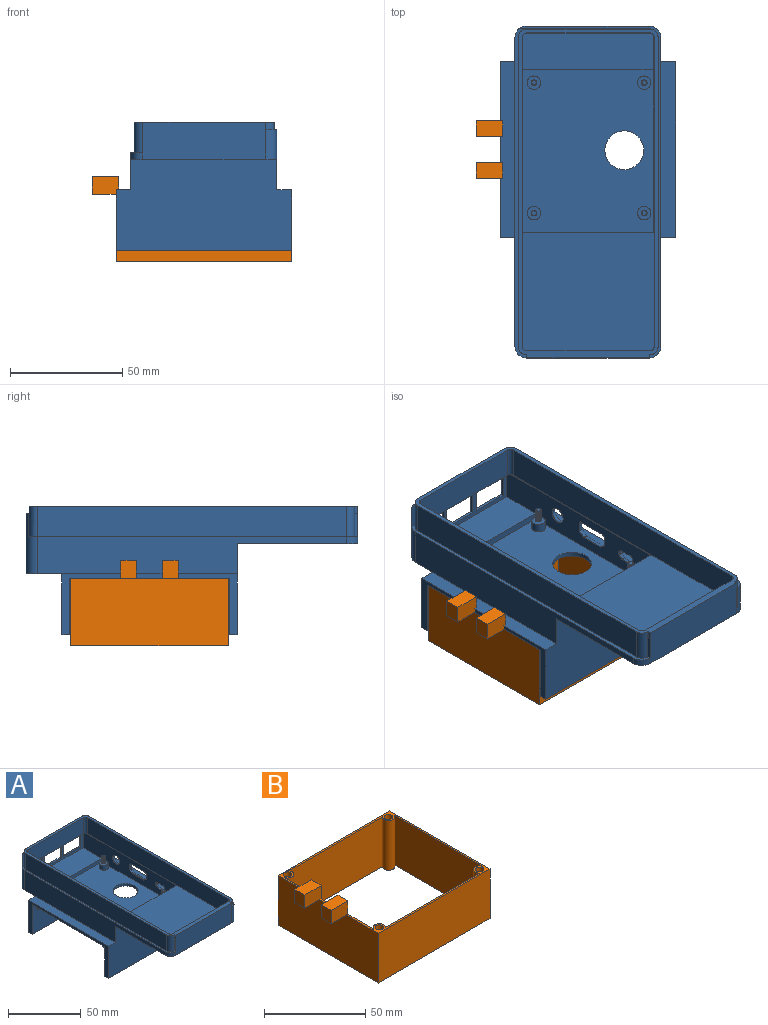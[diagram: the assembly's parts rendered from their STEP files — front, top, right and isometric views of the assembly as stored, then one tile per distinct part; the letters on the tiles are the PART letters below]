
ASSEMBLY  parts=2 mates=1
PART A: 172 faces, bbox 78.1x147.8x57.3 mm
  f0: plane 54.64x26.93mm, normal (0,1,0), area 672.3mm2, adj f70,f71,f72,f73,f74,f75,f76,f77
  f1: plane 10.44x0.05mm, normal (1,0,0), area 0.5mm2, adj f6,f156,f161,f168
  f2: plane 146.29x62.14mm, normal (0,0,1), area 777.6mm2, adj f3,f142,f143,f144,f145,f146,f147,f148
  f3: plane 54.77x16.64mm, normal (0,-1,0), area 908.8mm2, adj f2,f4,f5,f138,f139,f140,f163,f164
  f4: plane 10.44x1.35mm, normal (-1,0,0), area 14.1mm2, adj f3,f5,f147,f166
  f5: plane 146.45x5.23mm, normal (0,0,1), area 219.8mm2, adj f3,f4,f13,f69,f87,f136,f139,f145
  f6: plane 144.71x3.8mm, normal (0,0,1), area 7.4mm2, adj f1,f8,f142,f143,f156,f159,f160,f161
  f7: plane 137.44x26.93mm, normal (1,0,0), area 2509mm2, adj f10,f22,f70,f112,f113,f114,f115,f116
  f8: plane 90.66x16.5mm, normal (-1,0,0), area 1254.4mm2, adj f6,f9,f11,f12,f13,f83,f85,f88
  f9: plane 58.23x18.21mm, normal (0,0,1), area 1060.3mm2, adj f8,f12,f13,f87
  f10: plane 78x6.58mm, normal (0,0,1), area 513.2mm2, adj f7,f14,f20,f22
  f11: plane 72.45x58.92mm, normal (0,0,1), area 3922.5mm2, adj f8,f12,f44,f45,f46,f47,f68,f83
  f12: plane 58.92x3mm, normal (0,-1,0), area 176.8mm2, adj f8,f9,f11,f84,f86
  f13: plane 59.61x23.93mm, normal (0,-1,0), area 592.4mm2, adj f5,f8,f9,f71,f72,f73,f74,f75
  f14: plane 78x27mm, normal (0,1,0), area 2106mm2, adj f10,f20,f21,f23,f43,f70
  f15: plane 6.13x6.13mm, normal (0,0,1), area 24.4mm2, adj f44,f63,f65,f66,f67
  f16: plane 6.13x6.13mm, normal (0,0,1), area 24.4mm2, adj f46,f58,f60,f61,f62
  f17: plane 6.13x6.13mm, normal (0,0,1), area 24.4mm2, adj f47,f53,f55,f56,f57
  f18: plane 6.13x6.13mm, normal (0,0,1), area 24.4mm2, adj f45,f48,f50,f51,f52
  f19: plane 78x71mm, normal (0,0,-1), area 5254.4mm2, adj f20,f21,f24,f26,f32,f34,f40,f42
  f20: plane 78x27mm, normal (1,0,0), area 331mm2, adj f10,f14,f19,f22,f40,f41,f42,f43
  f21: plane 78x27mm, normal (-1,0,0), area 331mm2, adj f14,f19,f22,f23,f40,f41,f42,f43
  f22: plane 78x40.5mm, normal (0,-1,0), area 2981.2mm2, adj f7,f10,f20,f21,f23,f41,f69,f138
  f23: plane 78x6.58mm, normal (0,0,1), area 513.2mm2, adj f14,f21,f22,f69
  f24: cylinder r=2mm len=7mm, axis (0,0,1), area 88mm2, adj f19,f25
  f25: plane 4x4mm, normal (0,0,-1), area 10.6mm2, adj f24,f31
  f26: cylinder r=2mm len=7mm, axis (0,0,1), area 88mm2, adj f19,f27
  f27: plane 4x4mm, normal (0,0,-1), area 10.6mm2, adj f26,f29
  f28: cone r=0mm half-angle=59deg, axis (0,0,-1), area 2.3mm2, adj f29
  f29: cylinder r=0.8mm len=5.85mm, axis (0,0,-1), area 29.4mm2, adj f27,f28
  f30: cone r=0mm half-angle=59deg, axis (0,0,-1), area 2.3mm2, adj f31
  f31: cylinder r=0.8mm len=5.85mm, axis (0,0,-1), area 29.4mm2, adj f25,f30
  f32: cylinder r=2mm len=4mm, axis (0,0,1), area 37.7mm2, adj f19,f33
  f33: plane 4x4mm, normal (0,0,-1), area 10.6mm2, adj f32,f39
  f34: cylinder r=2mm len=4mm, axis (0,0,1), area 37.7mm2, adj f19,f35
  f35: plane 4x4mm, normal (0,0,-1), area 10.6mm2, adj f34,f37
  f36: cone r=0mm half-angle=59deg, axis (0,0,-1), area 2.3mm2, adj f37
  f37: cylinder r=0.8mm len=4mm, axis (0,0,-1), area 20.1mm2, adj f35,f36
  f38: cone r=0mm half-angle=59deg, axis (0,0,-1), area 2.3mm2, adj f39
  f39: cylinder r=0.8mm len=4mm, axis (0,0,-1), area 20.1mm2, adj f33,f38
  f40: plane 78x25mm, normal (0,1,0), area 1950mm2, adj f19,f20,f21,f41
  f41: plane 78x3.5mm, normal (0,0,-1), area 273mm2, adj f20,f21,f22,f40
  f42: plane 78x25mm, normal (0,-1,0), area 1950mm2, adj f19,f20,f21,f43
  f43: plane 78x3.5mm, normal (0,0,-1), area 273mm2, adj f14,f20,f21,f42
  f44: cylinder r=3mm len=6mm, axis (0,0,-1), area 75.4mm2, adj f11,f15
  f45: cylinder r=3mm len=6mm, axis (0,0,-1), area 75.4mm2, adj f11,f18
  f46: cylinder r=3mm len=6mm, axis (0,0,-1), area 75.4mm2, adj f11,f16
  f47: cylinder r=3mm len=6mm, axis (0,0,-1), area 75.4mm2, adj f11,f17
  f48: cylinder r=1.25mm len=6mm, axis (0,0,-1), area 27.4mm2, adj f18,f49,f50,f52
  f49: plane 2.35x2.35mm, normal (0,0,1), area 3.9mm2, adj f48,f50,f51,f52
  f50: bspline ~6.28x2.5mm, area 26.8mm2, adj f18,f48,f49,f51
  f51: cylinder r=1.01mm len=6mm, axis (0,0,-1), area -6.5mm2, adj f18,f49,f50,f52
  f52: bspline ~6.28x2.5mm, area 26.3mm2, adj f18,f48,f49,f51
  f53: cylinder r=1.25mm len=6mm, axis (0,0,-1), area 27.4mm2, adj f17,f54,f55,f57
  f54: plane 2.35x2.35mm, normal (0,0,1), area 3.9mm2, adj f53,f55,f56,f57
  f55: bspline ~6.28x2.5mm, area 26.8mm2, adj f17,f53,f54,f56
  f56: cylinder r=1.01mm len=6mm, axis (0,0,-1), area -6.5mm2, adj f17,f54,f55,f57
  f57: bspline ~6.28x2.5mm, area 26.3mm2, adj f17,f53,f54,f56
  f58: cylinder r=1.25mm len=6mm, axis (0,0,-1), area 27.4mm2, adj f16,f59,f60,f62
  f59: plane 2.35x2.35mm, normal (0,0,1), area 3.9mm2, adj f58,f60,f61,f62
  f60: bspline ~6.28x2.5mm, area 26.8mm2, adj f16,f58,f59,f61
  f61: cylinder r=1.01mm len=6mm, axis (0,0,-1), area -6.5mm2, adj f16,f59,f60,f62
  f62: bspline ~6.28x2.5mm, area 26.3mm2, adj f16,f58,f59,f61
  f63: cylinder r=1.25mm len=6mm, axis (0,0,-1), area 27.4mm2, adj f15,f64,f65,f67
  f64: plane 2.35x2.35mm, normal (0,0,1), area 3.9mm2, adj f63,f65,f66,f67
  f65: bspline ~6.28x2.5mm, area 26.8mm2, adj f15,f63,f64,f66
  f66: cylinder r=1.01mm len=6mm, axis (0,0,-1), area -6.5mm2, adj f15,f64,f65,f67
  f67: bspline ~6.28x2.5mm, area 26.3mm2, adj f15,f63,f64,f66
  f68: cylinder r=8.62mm len=17.24mm, axis (0,0,1), area 108.3mm2, adj f11,f19
  f69: plane 137.44x16.5mm, normal (-1,0,0), area 1611.1mm2, adj f5,f22,f23,f70,f136,f138,f139
  f70: plane 64.84x15.91mm, normal (0,0,-1), area 1020.3mm2, adj f0,f7,f14,f69,f136,f137
  f71: plane 17x1.2mm, normal (-1,0,0), area 20.4mm2, adj f0,f13,f72,f73
  f72: plane 16.28x1.2mm, normal (0,0,-1), area 19.5mm2, adj f0,f13,f71,f74
  f73: plane 16.4x1.2mm, normal (0,0,1), area 19.6mm2, adj f0,f13,f71,f74
  f74: plane 17x1.2mm, normal (1,0,-0.01), area 20.4mm2, adj f0,f13,f72,f73
  f75: plane 16.28x1.2mm, normal (0,0,-1), area 19.5mm2, adj f0,f13,f76,f77
  f76: plane 17x1.2mm, normal (1,0,0), area 20.4mm2, adj f0,f13,f75,f78
  f77: plane 17x1.2mm, normal (-1,0,0), area 20.4mm2, adj f0,f13,f75,f78
  f78: plane 16.29x1.2mm, normal (0,0,1), area 19.5mm2, adj f0,f13,f76,f77
  f79: plane 14.5x1.2mm, normal (1,0,0), area 17.4mm2, adj f0,f13,f80,f82
  f80: plane 16.88x1.2mm, normal (0,0,-1), area 20.2mm2, adj f0,f13,f79,f81
  f81: plane 14.5x1.2mm, normal (-1,0,0), area 17.4mm2, adj f0,f13,f80,f82
  f82: plane 16.88x1.2mm, normal (0,0,1), area 20.2mm2, adj f0,f13,f79,f81
  f83: plane 58.92x16.5mm, normal (0,1,0), area 962.7mm2, adj f8,f11,f84,f85,f86,f87,f141
  f84: plane 72.45x3mm, normal (1,0,0), area 217.3mm2, adj f11,f12,f83,f86
  f85: plane 140.7x58.64mm, normal (0,0,1), area 3126.7mm2, adj f8,f83,f148,f149,f150,f151,f152,f153
  f86: plane 72.45x0.7mm, normal (0,0,-1), area 50.6mm2, adj f12,f83,f84,f87
  f87: plane 90.66x13.5mm, normal (1,0,0), area 1223.8mm2, adj f5,f9,f13,f83,f86,f141
  f88: plane 1.91x0.42mm, normal (0,0,-1), area 0.8mm2, adj f8,f89,f134
  f89: cylinder r=3.48mm len=6.95mm, axis (1,0,0), area 8.3mm2, adj f8,f88,f135
  f90: cylinder r=1.5mm len=1.5mm, axis (1,0,0), area 1mm2, adj f8,f91,f95,f128
  f91: plane 12.99x0.42mm, normal (0,0,-1), area 5.4mm2, adj f8,f90,f92,f126
  f92: cylinder r=1.5mm len=1.5mm, axis (1,0,0), area 1mm2, adj f8,f91,f93,f127
  f93: plane 4.06x0.42mm, normal (0,1,0), area 1.7mm2, adj f8,f92,f94,f129
  f94: plane 2.59x1.94mm, normal (0,0.6,0.8), area 1.3mm2, adj f8,f93,f96,f131
  f95: plane 4.06x0.42mm, normal (0,-1,0), area 1.7mm2, adj f8,f90,f97,f130
  f96: plane 10.81x0.42mm, normal (0,0,1), area 4.5mm2, adj f8,f94,f97,f133
  f97: plane 2.59x1.94mm, normal (0,-0.6,0.8), area 1.3mm2, adj f8,f95,f96,f132
  f98: plane 5.68x0.42mm, normal (0,0,1), area 2.4mm2, adj f8,f99,f111,f123
  f99: plane 1.54x1.21mm, normal (0,-0.79,0.62), area 0.8mm2, adj f8,f98,f100,f125
  f100: cylinder r=1mm len=0.62mm, axis (1,0,0), area 0.3mm2, adj f8,f99,f101,f124
  f101: plane 0.93x0.42mm, normal (0,-1,0), area 0.4mm2, adj f8,f100,f102,f122
  f102: cylinder r=1mm len=0.71mm, axis (1,0,0), area 0.3mm2, adj f8,f101,f103,f120
  f103: plane 0.47x0.47mm, normal (0,-0.71,-0.71), area 0.3mm2, adj f8,f102,f104,f118
  f104: cylinder r=1mm len=0.71mm, axis (1,0,0), area 0.3mm2, adj f8,f103,f105,f116
  f105: plane 5.59x0.42mm, normal (0,0,-1), area 2.3mm2, adj f8,f104,f106,f114
  f106: cylinder r=1mm len=0.71mm, axis (1,0,0), area 0.3mm2, adj f8,f105,f107,f112
  f107: plane 0.47x0.47mm, normal (0,0.71,-0.71), area 0.3mm2, adj f8,f106,f108,f113
  f108: cylinder r=1mm len=0.71mm, axis (1,0,0), area 0.3mm2, adj f8,f107,f109,f115
  f109: plane 0.93x0.42mm, normal (0,1,0), area 0.4mm2, adj f8,f108,f110,f117
  f110: cylinder r=1mm len=0.62mm, axis (1,0,0), area 0.3mm2, adj f8,f109,f111,f119
  f111: plane 1.54x1.21mm, normal (0,0.79,0.62), area 0.8mm2, adj f8,f98,f110,f121
  f112: torus R=4mm, axis (-1,0,0), area 7.7mm2, adj f7,f106,f113,f114
  f113: cylinder r=3mm len=3mm, axis (0,-0.71,-0.71), area 3.1mm2, adj f7,f107,f112,f115
  f114: cylinder r=3mm len=5.59mm, axis (0,-1,0), area 26.4mm2, adj f7,f105,f112,f116
  f115: torus R=4mm, axis (-1,0,0), area 7.7mm2, adj f7,f108,f113,f117
  f116: torus R=4mm, axis (-1,0,0), area 7.7mm2, adj f7,f104,f114,f118
  f117: cylinder r=3mm len=3mm, axis (0,0,-1), area 4.4mm2, adj f7,f109,f115,f119
  f118: cylinder r=3mm len=3mm, axis (0,-0.71,0.71), area 3.1mm2, adj f7,f103,f116,f120
  f119: torus R=4mm, axis (-1,0,0), area 6.6mm2, adj f7,f110,f117,f121
  f120: torus R=4mm, axis (-1,0,0), area 7.7mm2, adj f7,f102,f118,f122
  f121: cylinder r=3mm len=4.54mm, axis (0,0.62,-0.79), area 12.7mm2, adj f7,f111,f119,f123
  f122: cylinder r=3mm len=3mm, axis (0,0,1), area 4.4mm2, adj f7,f101,f120,f124
  f123: cylinder r=3mm len=8.59mm, axis (0,1,0), area 33.6mm2, adj f7,f98,f121,f125
  f124: torus R=4mm, axis (-1,0,0), area 6.6mm2, adj f7,f100,f122,f125
  f125: cylinder r=3mm len=4.54mm, axis (0,0.62,0.79), area 12.7mm2, adj f7,f99,f123,f124
  f126: cylinder r=3mm len=12.99mm, axis (0,-1,0), area 61.2mm2, adj f7,f91,f127,f128
  f127: torus R=4.5mm, axis (-1,0,0), area 19.2mm2, adj f7,f92,f126,f129
  f128: torus R=4.5mm, axis (-1,0,0), area 19.2mm2, adj f7,f90,f126,f130
  f129: cylinder r=3mm len=5.55mm, axis (0,0,-1), area 22.6mm2, adj f7,f93,f127,f131
  f130: cylinder r=3mm len=5.55mm, axis (0,0,1), area 22.6mm2, adj f7,f95,f128,f132
  f131: cylinder r=3mm len=6.39mm, axis (0,0.8,-0.6), area 21.1mm2, adj f7,f94,f129,f133
  f132: cylinder r=3mm len=6.39mm, axis (0,0.8,0.6), area 21.1mm2, adj f7,f97,f130,f133
  f133: cylinder r=3mm len=12.81mm, axis (0,1,0), area 55.7mm2, adj f7,f96,f131,f132
  f134: cylinder r=3mm len=3mm, axis (0,-1,0), area 10.7mm2, adj f7,f88,f135
  f135: torus R=6.48mm, axis (-1,0,0), area 125.1mm2, adj f7,f89,f134
  f136: cylinder r=5.1mm len=26.93mm, axis (0,0,1), area 169.4mm2, adj f0,f5,f13,f69,f70,f158
  f137: cylinder r=5.1mm len=26.93mm, axis (0,0,1), area 215.8mm2, adj f0,f7,f70,f158
  f138: plane 64.84x53.73mm, normal (0,0,-1), area 3472.9mm2, adj f3,f7,f22,f69,f139,f140
  f139: cylinder r=5.1mm len=5.1mm, axis (0,0,1), area 24mm2, adj f3,f5,f69,f138
  f140: cylinder r=5.1mm len=13.44mm, axis (0,0,1), area 106.3mm2, adj f3,f7,f138,f158,f163,f164
  f141: plane 90.51x58.23mm, normal (0,0,-1), area 105.2mm2, adj f8,f83,f87,f143,f144,f145,f148,f153
  f142: plane 137.44x13.64mm, normal (1,0,0), area 1874mm2, adj f2,f6,f143,f156
  f143: cylinder r=3.75mm len=13.64mm, axis (0,0,-1), area 80.3mm2, adj f2,f6,f141,f142,f144
  f144: plane 54.64x13.64mm, normal (0,1,0), area 745mm2, adj f2,f141,f143,f145
  f145: cylinder r=3.75mm len=13.64mm, axis (0,0,-1), area 80.3mm2, adj f2,f5,f141,f144,f146
  f146: plane 137.44x13.64mm, normal (-1,0,0), area 1874mm2, adj f2,f5,f145,f147
  f147: cylinder r=3.75mm len=13.64mm, axis (0,0,-1), area 80.3mm2, adj f2,f4,f5,f146,f165
  f148: cylinder r=2mm len=13.64mm, axis (0,0,-1), area 42.8mm2, adj f2,f85,f141,f149,f155
  f149: plane 137.44x13.64mm, normal (-1,0,0), area 1874mm2, adj f2,f85,f148,f150
  f150: cylinder r=2mm len=13.64mm, axis (0,0,-1), area 42.8mm2, adj f2,f85,f149,f151
  f151: plane 54.64x13.64mm, normal (0,1,0), area 745mm2, adj f2,f85,f150,f152
  f152: cylinder r=2mm len=13.64mm, axis (0,0,-1), area 42.8mm2, adj f2,f85,f151,f153
  f153: plane 137.44x13.64mm, normal (1,0,0), area 1874mm2, adj f2,f85,f141,f152,f154
  f154: cylinder r=2mm len=13.64mm, axis (0,0,-1), area 42.8mm2, adj f2,f141,f153,f155
  f155: plane 54.64x13.64mm, normal (0,-1,0), area 745mm2, adj f2,f141,f148,f154
  f156: cylinder r=3.75mm len=13.64mm, axis (0,0,-1), area 80.3mm2, adj f1,f2,f6,f142,f169
  f157: plane 1.55x0.44mm, normal (0,0,-1), area 0.3mm2, adj f8,f13,f159,f162
  f158: plane 147.64x63.02mm, normal (0,0,1), area 246.1mm2, adj f0,f7,f13,f136,f137,f140,f159,f160
  f159: cylinder r=3.8mm len=10.44mm, axis (0,0,-1), area 62.3mm2, adj f6,f157,f158,f160,f162
  f160: plane 137.44x10.44mm, normal (-1,0,0), area 1434.2mm2, adj f6,f158,f159,f161
  f161: cylinder r=3.8mm len=10.44mm, axis (0,0,-1), area 62.3mm2, adj f1,f6,f158,f160
  f162: plane 10.44x0.1mm, normal (-1,0,0), area 1.1mm2, adj f13,f157,f158,f159
  f163: plane 13.64x1.3mm, normal (1,0,0), area 4.2mm2, adj f2,f3,f140,f158,f164,f170
  f164: plane 0.13x0mm, normal (0,0,-1), area 0mm2, adj f3,f140,f163
  f165: plane 3.2x0.05mm, normal (0,-1,0), area 0.2mm2, adj f2,f147,f166,f167
  f166: plane 1.35x0.05mm, normal (0,0,1), area 0.1mm2, adj f3,f4,f165,f167
  f167: plane 3.2x1.35mm, normal (-1,0,0), area 4.3mm2, adj f2,f3,f165,f166
  f168: plane 0.05x0.05mm, normal (0,0,1), area 0mm2, adj f1,f169,f170,f171
  f169: plane 3.2x0.05mm, normal (0,-1,0), area 0.2mm2, adj f2,f156,f168,f171
  f170: plane 3.2x0.05mm, normal (0,1,0), area 0.2mm2, adj f2,f163,f168,f171
  f171: plane 3.2x0.05mm, normal (1,0,0), area 0.2mm2, adj f2,f168,f169,f170
PART B: 33 faces, bbox 88.6x70x38 mm
  f0: plane 11.64x1mm, normal (0,0,1), area 11.6mm2, adj f2,f10,f22,f30
  f1: plane 78x70mm, normal (0,0,1), area 320mm2, adj f2,f3,f4,f5,f6,f7,f8,f9
  f2: plane 62.4x30mm, normal (1,0,0), area 1872.1mm2, adj f0,f1,f3,f17,f18,f19,f26
  f3: cylinder r=3.12mm len=30mm, axis (0,0,1), area 319.6mm2, adj f1,f2,f4,f18
  f4: plane 65.18x30mm, normal (0,-1,0), area 1955.4mm2, adj f1,f3,f5,f18
  f5: cylinder r=3.12mm len=30mm, axis (0,0,1), area 343.4mm2, adj f1,f4,f6,f18
  f6: plane 61.79x30mm, normal (-1,0,0), area 1853.6mm2, adj f1,f5,f7,f18
  f7: cylinder r=3.12mm len=30mm, axis (0,0,1), area 343.4mm2, adj f1,f6,f8,f18
  f8: plane 65.68x30mm, normal (0,1,0), area 1970.3mm2, adj f1,f7,f17,f18
  f9: plane 78x30mm, normal (0,1,0), area 2340mm2, adj f1,f10,f16,f18
  f10: plane 70x30mm, normal (-1,0,0), area 2100mm2, adj f0,f1,f9,f11,f18,f24,f31
  f11: plane 78x30mm, normal (0,-1,0), area 2340mm2, adj f1,f10,f16,f18
  f12: cylinder r=2.12mm len=30mm, axis (0,0,1), area 399.6mm2, adj f1,f18
  f13: cylinder r=2.12mm len=30mm, axis (0,0,1), area 399.6mm2, adj f1,f18
  f14: cylinder r=2.12mm len=30mm, axis (0,0,1), area 399.6mm2, adj f1,f18
  f15: cylinder r=2.12mm len=30mm, axis (0,0,1), area 399.6mm2, adj f1,f18
  f16: plane 70x30mm, normal (1,0,0), area 2100mm2, adj f1,f9,f11,f18
  f17: cylinder r=3.12mm len=30mm, axis (0,0,1), area 343.4mm2, adj f1,f2,f8,f18
  f18: plane 78x70mm, normal (0,0,-1), area 345.5mm2, adj f2,f3,f4,f5,f6,f7,f8,f9
  f19: plane 6.93x0.05mm, normal (0,0,-1), area 0.3mm2, adj f2,f20,f21,f22
  f20: plane 11.6x8mm, normal (0,-1,0), area 92.8mm2, adj f1,f19,f21,f23,f24,f25
  f21: plane 8x6.93mm, normal (1,0,0), area 55.5mm2, adj f19,f20,f22,f25
  f22: plane 11.6x8mm, normal (0,1,0), area 92.8mm2, adj f0,f19,f21,f23,f24,f25
  f23: plane 8x6.93mm, normal (-1,0,0), area 55.5mm2, adj f20,f22,f24,f25
  f24: plane 10.55x6.93mm, normal (0,0,-1), area 73.2mm2, adj f10,f20,f22,f23
  f25: plane 11.6x6.93mm, normal (0,0,1), area 80.4mm2, adj f20,f21,f22,f23
  f26: plane 6.93x0.05mm, normal (0,0,-1), area 0.3mm2, adj f2,f27,f28,f30
  f27: plane 8x6.93mm, normal (1,0,0), area 55.5mm2, adj f26,f28,f30,f32
  f28: plane 11.6x8mm, normal (0,1,0), area 92.8mm2, adj f1,f26,f27,f29,f31,f32
  f29: plane 8x6.93mm, normal (-1,0,0), area 55.5mm2, adj f28,f30,f31,f32
  f30: plane 11.6x8mm, normal (0,-1,0), area 92.8mm2, adj f0,f26,f27,f29,f31,f32
  f31: plane 10.55x6.93mm, normal (0,0,-1), area 73.2mm2, adj f10,f28,f29,f30
  f32: plane 11.6x6.93mm, normal (0,0,1), area 80.4mm2, adj f27,f28,f29,f30
PLACE A t=(4,7.25,-2)mm fixed
PLACE B t=(4,7.25,-2)mm
MATE slider A.f19 <-> B.f1  axis (0,0,-1) through (78,39,-2)mm
